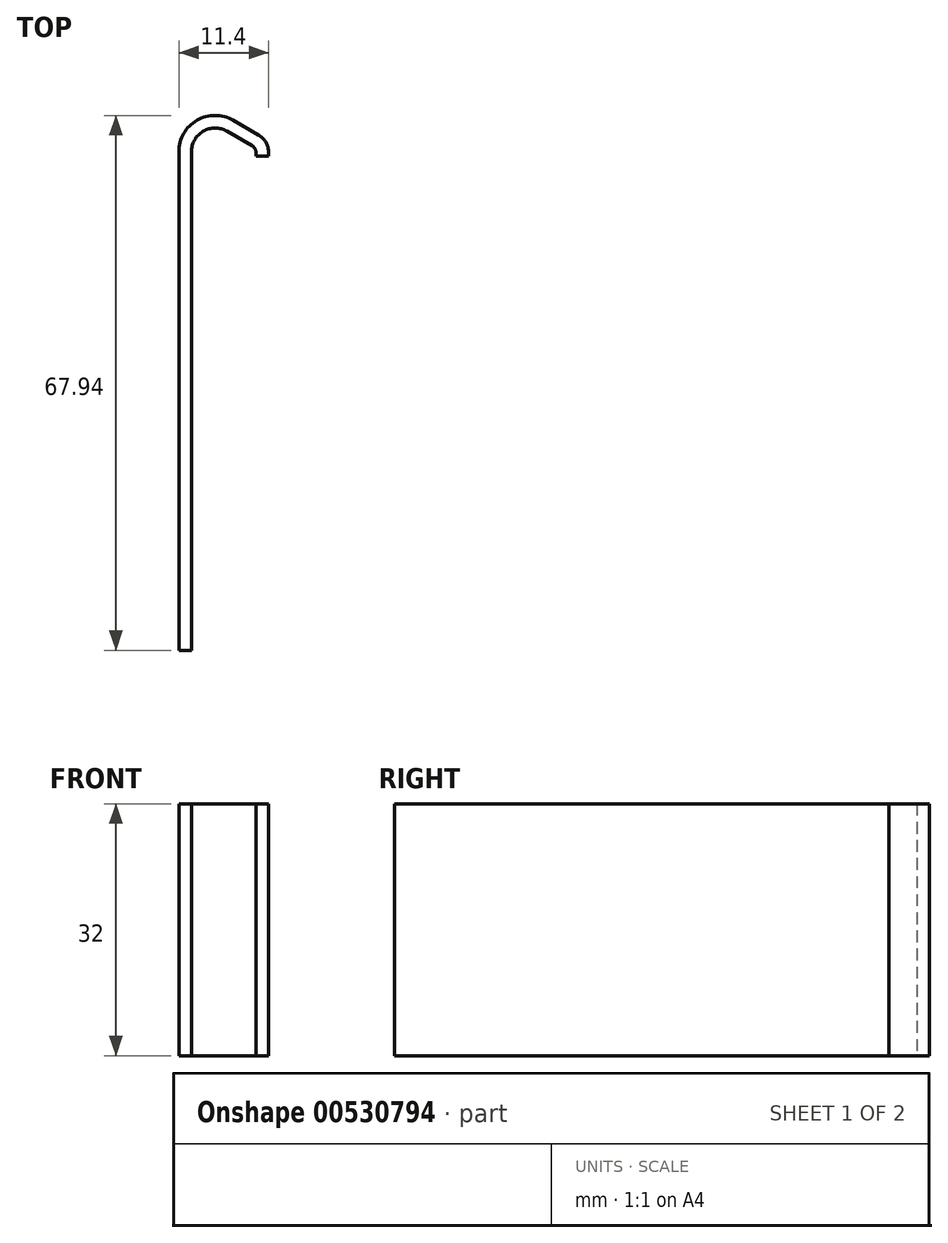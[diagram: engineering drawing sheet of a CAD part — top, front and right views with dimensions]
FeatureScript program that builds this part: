
annotation { "Feature Type Name" : "Feature", "Feature Type Description" : "" }
export const myFeature = defineFeature(function(context is Context, id is Id, definition is map)
    precondition{}
    {
        {
            var Q0;
            Q0=qCreatedBy(makeId("Top.planeOp"),FACE);
            var sketch = newSketch(context, id + "F0", { "sketchPlane" : qUnion([Q0])});
            skLineSegment(sketch, "E0", {"start": v(-6.8, -55.4) * mm, "end": v(-5.2, -55.4) * mm});
            skLineSegment(sketch, "E1", {"start": v(-5.2, -55.4) * mm, "end": v(-5.2, 7.95) * mm});
            skLineSegment(sketch, "E2", {"start": v(-0.7, 10.54) * mm, "end": v(2.5, 8.7) * mm});
            skLineSegment(sketch, "E3", {"start": v(3, 7.83) * mm, "end": v(3, 7.4) * mm});
            skLineSegment(sketch, "E4", {"start": v(3, 7.4) * mm, "end": v(4.6, 7.4) * mm});
            skLineSegment(sketch, "E5", {"start": v(4.6, 7.4) * mm, "end": v(4.6, 7.83) * mm});
            skLineSegment(sketch, "E6", {"start": v(3.3, 10.08) * mm, "end": v(0.1, 11.93) * mm});
            skLineSegment(sketch, "E7", {"start": v(-6.8, 7.95) * mm, "end": v(-6.8, -55.4) * mm});
            skArc(sketch, "E8", {"start": v(-0.7, 10.54) * mm, "mid": v(-3.7, 10.54) * mm, "end": v(-5.2, 7.95) * mm});
            skArc(sketch, "E9", {"start": v(0.1, 11.93) * mm, "mid": v(-4.5, 11.93) * mm, "end": v(-6.8, 7.95) * mm});
            skArc(sketch, "E10", {"start": v(4.6, 7.83) * mm, "mid": v(4.25, 9.13) * mm, "end": v(3.3, 10.08) * mm});
            skArc(sketch, "E11", {"start": v(3, 7.83) * mm, "mid": v(2.86, 8.33) * mm, "end": v(2.5, 8.7) * mm});
            skLineSegment(sketch, "E12", {"start": v(2.5, 8.7) * mm, "end": v(3, 8.4) * mm, "construction": true});
            skLineSegment(sketch, "E13", {"start": v(3, 8.4) * mm, "end": v(3, 7.83) * mm, "construction": true});
            skLineSegment(sketch, "E14", {"start": v(3, 8.4) * mm, "end": v(-5.2, 7.95) * mm, "construction": true});
            skSolve(sketch);
        }
        {
            var Q0;
            Q0=makeQuery(id+"F0.imprint","IMPRINT",FACE,{"disambiguationData":[TD([[makeQuery(id+"F0.imprint","IMPRINT",EDGE,{"derivedFrom":sQuery(id+"F0.wireOp",EDGE,"E0")}),1.0]])]});
            extrude(context, id + "F1", {"entities" : qUnion([Q0]), "depth" : 32 * mm, "offsetDistance" : 25 * mm});
        }
    });
